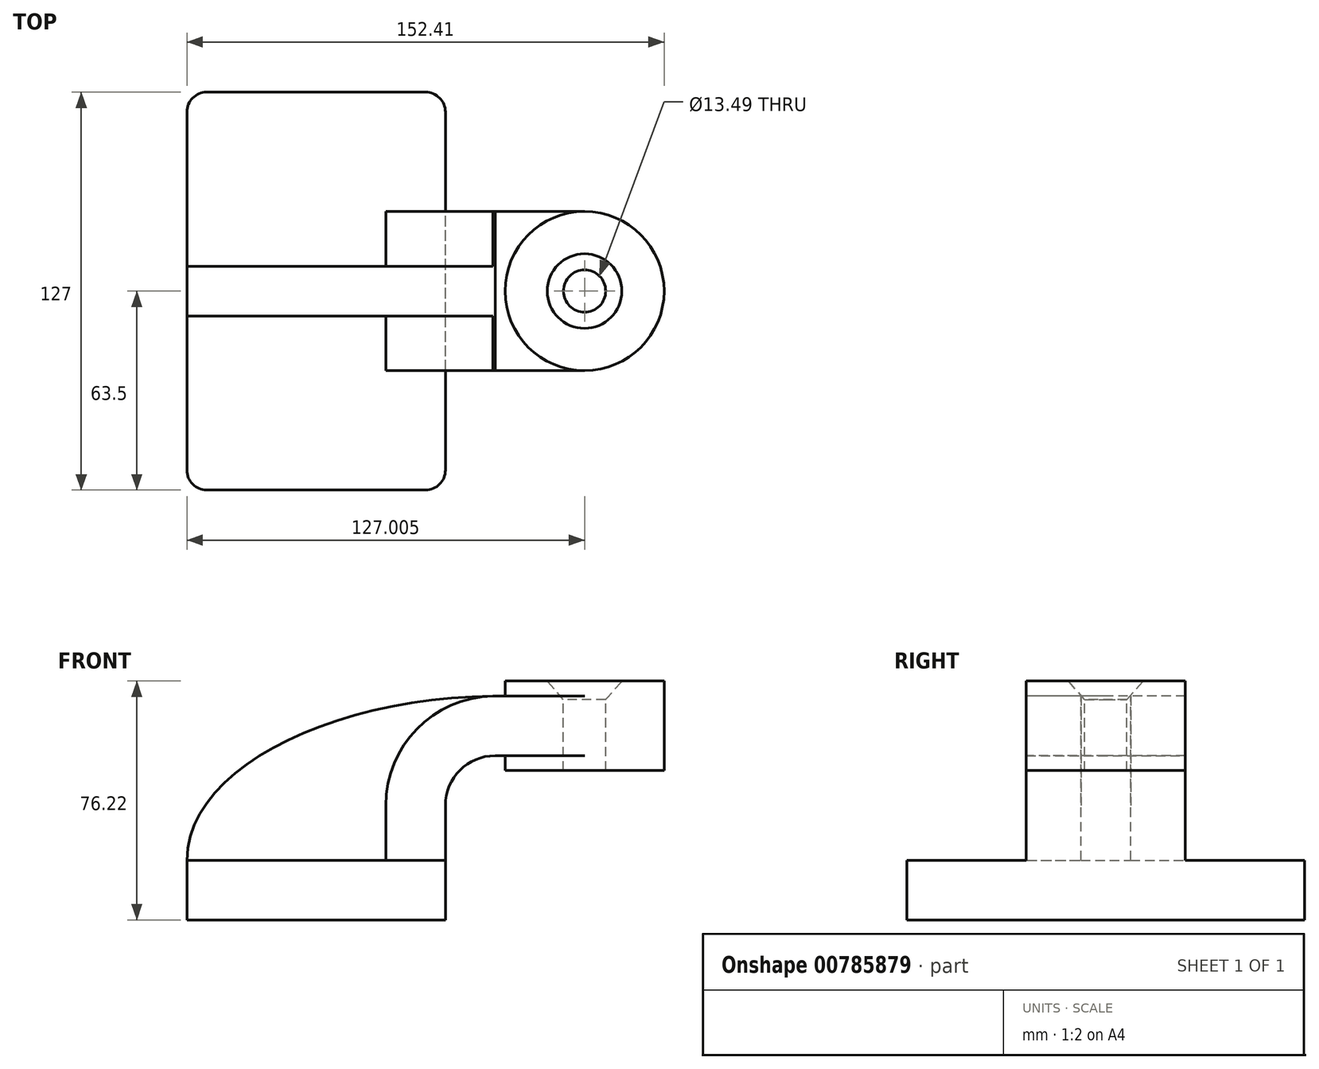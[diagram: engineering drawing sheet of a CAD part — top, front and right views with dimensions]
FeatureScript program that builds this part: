
annotation { "Feature Type Name" : "Feature", "Feature Type Description" : "" }
export const myFeature = defineFeature(function(context is Context, id is Id, definition is map)
    precondition{}
    {
        {
            var Q0;
            Q0=qCreatedBy(makeId("Front.planeOp"),FACE);
            var sketch = newSketch(context, id + "F0", { "sketchPlane" : qUnion([Q0])});
            skLineSegment(sketch, "E0.bottom", {"start": v(-41.28, -9.52) * mm, "end": v(41.28, -9.52) * mm});
            skLineSegment(sketch, "E0.top", {"start": v(-41.28, 9.53) * mm, "end": v(41.28, 9.53) * mm});
            skLineSegment(sketch, "E0.left", {"start": v(-41.28, -9.52) * mm, "end": v(-41.28, 9.53) * mm});
            skLineSegment(sketch, "E0.right", {"start": v(41.28, -9.52) * mm, "end": v(41.28, 9.53) * mm});
            skPoint(sketch, "E0.middle", {"position": v(0, 0) * mm});
            skLineSegment(sketch, "E1.bottom", {"start": v(60.33, 38.11) * mm, "end": v(111.12, 38.11) * mm});
            skLineSegment(sketch, "E1.top", {"start": v(60.32, 66.69) * mm, "end": v(111.12, 66.69) * mm});
            skLineSegment(sketch, "E1.left", {"start": v(60.32, 38.11) * mm, "end": v(60.32, 66.69) * mm});
            skLineSegment(sketch, "E1.right", {"start": v(111.12, 38.11) * mm, "end": v(111.12, 66.69) * mm});
            skPoint(sketch, "E1.middle", {"position": v(85.72, 52.4) * mm});
            skLineSegment(sketch, "E2", {"start": v(41.27, 9.53) * mm, "end": v(41.27, 27) * mm});
            skArc(sketch, "E3", {"start": v(41.27, 27) * mm, "mid": v(45.92, 38.23) * mm, "end": v(57.15, 42.88) * mm});
            skLineSegment(sketch, "E4", {"start": v(57.15, 42.88) * mm, "end": v(93.27, 42.88) * mm});
            skLineSegment(sketch, "E5.0", {"start": v(57.15, 61.93) * mm, "end": v(93.27, 61.93) * mm});
            skArc(sketch, "E5.1", {"start": v(22.22, 27) * mm, "mid": v(32.45, 51.7) * mm, "end": v(57.15, 61.93) * mm});
            skLineSegment(sketch, "E5.2", {"start": v(22.22, 9.53) * mm, "end": v(22.22, 27) * mm});
            skLineSegment(sketch, "E6", {"start": v(85.72, 38.11) * mm, "end": v(85.72, 66.69) * mm});
            skFitSpline(sketch, "E7", {"points": [v(-41.28, 9.53) * mm, v(57.15, 61.93) * mm], "startDerivative": vector(1.01, 90.06) * mm, "endDerivative": vector(153.29, 1.3) * mm});
            skSolve(sketch);
        }
        {
            var Q0;
            Q0=makeQuery(id+"F0.imprint","IMPRINT",FACE,{"disambiguationData":[TD([[makeQuery(id+"F0.imprint","IMPRINT",EDGE,{"derivedFrom":sQuery(id+"F0.wireOp",EDGE,"E0.bottom")}),1.0]])]});
            extrude(context, id + "F1", {"entities" : qUnion([Q0]), "endBound" : BoundingType.SYMMETRIC, "depth" : 127 * mm, "offsetDistance" : 25.4 * mm});
        }
        {
            var Q0;
            {var subQ1=sQuery(id+"F0.wireOp",EDGE,"E2");Q0=makeQuery(id+"F0.imprint","IMPRINT",FACE,{"disambiguationData":[TD([[makeQuery(id+"F0.imprint","IMPRINT",EDGE,{"derivedFrom":subQ1}),1.0]])]});}
            var Q1;
            {var subQ0=sQuery(id+"F0.wireOp",EDGE,"E4");var subQ1=sQuery(id+"F0.wireOp",EDGE,"E1.left");var subQ2=makeQuery(id+"F0.imprint","INTERSECT",VERTEX,{"derivedFrom":[subQ1,subQ0]});Q1=makeQuery(id+"F0.imprint","IMPRINT",FACE,{"disambiguationData":[TD([[makeQuery(id+"F0.imprint","IMPRINT",EDGE,{"disambiguationData":[TD([[subQ2,-1.0]])],"derivedFrom":subQ1}),-1.0]])]});}
            extrude(context, id + "F2", {"entities" : qUnion([Q0, Q1]), "operationType" : NewBodyOperationType.ADD, "endBound" : BoundingType.SYMMETRIC, "depth" : 50.8 * mm, "offsetDistance" : 25.4 * mm});
        }
        {
            var Q0;
            {var subQ3=sQuery(id+"F0.wireOp",EDGE,"E5.2");Q0=makeQuery(id+"F0.imprint","IMPRINT",FACE,{"disambiguationData":[TD([[makeQuery(id+"F0.imprint","IMPRINT",EDGE,{"derivedFrom":subQ3}),1.0]])]});}
            extrude(context, id + "F3", {"entities" : qUnion([Q0]), "operationType" : NewBodyOperationType.ADD, "endBound" : BoundingType.SYMMETRIC, "depth" : 15.88 * mm, "offsetDistance" : 25.4 * mm});
        }
        {
            var Q0;
            {var subQ4=sQuery(id+"F0.wireOp",EDGE,"E1.right");Q0=makeQuery(id+"F0.imprint","IMPRINT",FACE,{"disambiguationData":[TD([[makeQuery(id+"F0.imprint","IMPRINT",EDGE,{"derivedFrom":subQ4}),1.0]])]});}
            var Q1;
            Q1=sQuery(id+"F0.wireOp",EDGE,"E6");
            revolve(context, id + "F4", {"operationType" : NewBodyOperationType.ADD, "surfaceOperationType" : NewSurfaceOperationType.NEW, "entities" : qUnion([Q0]), "axis" : qUnion([Q1]), "revolveType" : RevolveType.FULL});
        }
        {
            var Q0;
            Q0=makeQuery(id+"F1.opExtrude","CAP_EDGE",EDGE,{"disambiguationData":[OSD([sQuery(id+"F0.wireOp",EDGE,"E0.left")])],"isStart":false});
            var Q1;
            Q1=makeQuery(id+"F1.opExtrude","CAP_EDGE",EDGE,{"disambiguationData":[OSD([sQuery(id+"F0.wireOp",EDGE,"E0.right")])],"isStart":false});
            var Q2;
            Q2=makeQuery(id+"F1.opExtrude","CAP_EDGE",EDGE,{"disambiguationData":[OSD([sQuery(id+"F0.wireOp",EDGE,"E0.right")])],"isStart":true});
            var Q3;
            Q3=makeQuery(id+"F1.opExtrude","CAP_EDGE",EDGE,{"disambiguationData":[OSD([sQuery(id+"F0.wireOp",EDGE,"E0.left")])],"isStart":true});
            fillet(context, id + "F5", {"entities" : qUnion([Q0, Q1, Q2, Q3]), "radius" : 6.35 * mm, "tangentPropagation" : true, "allowEdgeOverflow" : false});
        }
        {
            var Q0;
            Q0=makeQuery(id+"F4.opRevolve","SWEPT_FACE",FACE,{"disambiguationData":[OSD([sQuery(id+"F0.wireOp",EDGE,"E1.top")])]});
            var sketch = newSketch(context, id + "F6", { "sketchPlane" : qUnion([Q0])});
            skCircle(sketch, "E8", {"center": v(85.72, 0) * mm, "radius": 15.31 * mm});
            skSolve(sketch);
        }
        {
            var Q0;
            Q0=sQuery(id+"F6.wireOp",VERTEX,"E8.center");
            var Q1;
            Q1=makeQuery(id+"F1.opExtrude","SWEPT_BODY",BODY,{"disambiguationData":[OSD([sQuery(id+"F0.wireOp",EDGE,"E0.bottom"),sQuery(id+"F0.wireOp",EDGE,"E0.top"),sQuery(id+"F0.wireOp",EDGE,"E0.left"),sQuery(id+"F0.wireOp",EDGE,"E0.right")])]});
            hole(context, id + "F7", {"style" : HoleStyle.C_SINK, "endStyle" : HoleEndStyle.THROUGH, "standardTappedOrClearance" : lookupTablePath({ "standard" : "ANSI", "fit" : "Normal (ASME)", "size" : "1/2", "type" : "Clearance" }), "standardBlindInLast" : lookupTablePath({ "fit" : "Free", "standard" : "ANSI", "size" : "1/2", "type" : "Clearance" }), "holeDiameter" : 13.5 * mm, "cSinkDiameter" : 23.83 * mm, "cSinkAngle" : 82 * degree, "majorDiameter" : 6.35 * mm, "isTappedThrough" : true, "tappedDepth" : 12.7 * mm, "tapClearance" : 3, "locations" : qUnion([Q0]), "scope" : qUnion([Q1])});
        }
    });
